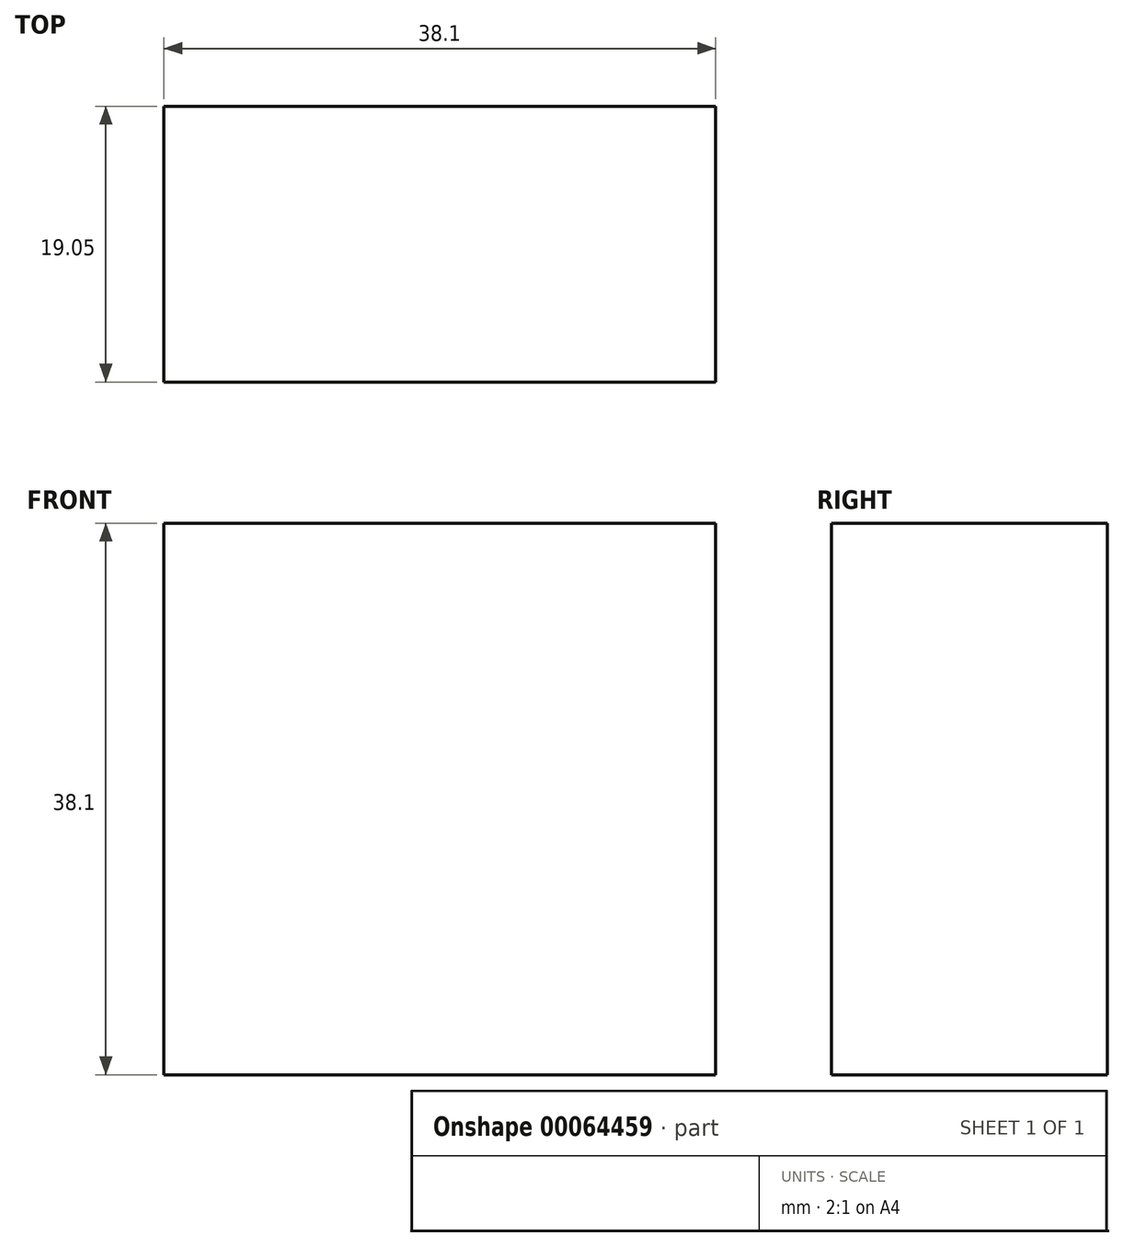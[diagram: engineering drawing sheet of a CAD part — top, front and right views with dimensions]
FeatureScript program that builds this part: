
annotation { "Feature Type Name" : "Feature", "Feature Type Description" : "" }
export const myFeature = defineFeature(function(context is Context, id is Id, definition is map)
    precondition{}
    {
        {
            var Q0;
            Q0=qCreatedBy(makeId("Front.planeOp"),FACE);
            var sketch = newSketch(context, id + "F0", { "sketchPlane" : qUnion([Q0])});
            skLineSegment(sketch, "E0.bottom", {"start": v(0, 0) * mm, "end": v(38.1, 0) * mm});
            skLineSegment(sketch, "E0.top", {"start": v(0, 38.1) * mm, "end": v(38.1, 38.1) * mm});
            skLineSegment(sketch, "E0.left", {"start": v(0, 0) * mm, "end": v(0, 38.1) * mm});
            skLineSegment(sketch, "E0.right", {"start": v(38.1, 0) * mm, "end": v(38.1, 38.1) * mm});
            skSolve(sketch);
        }
        {
            var Q0;
            Q0=makeQuery(id+"F0.imprint","IMPRINT",FACE,{"disambiguationData":[TD([[makeQuery(id+"F0.imprint","IMPRINT",EDGE,{"derivedFrom":sQuery(id+"F0.wireOp",EDGE,"E0.bottom")}),1.0]])]});
            extrude(context, id + "F1", {"entities" : qUnion([Q0]), "depth" : 19.05 * mm});
        }
    });
